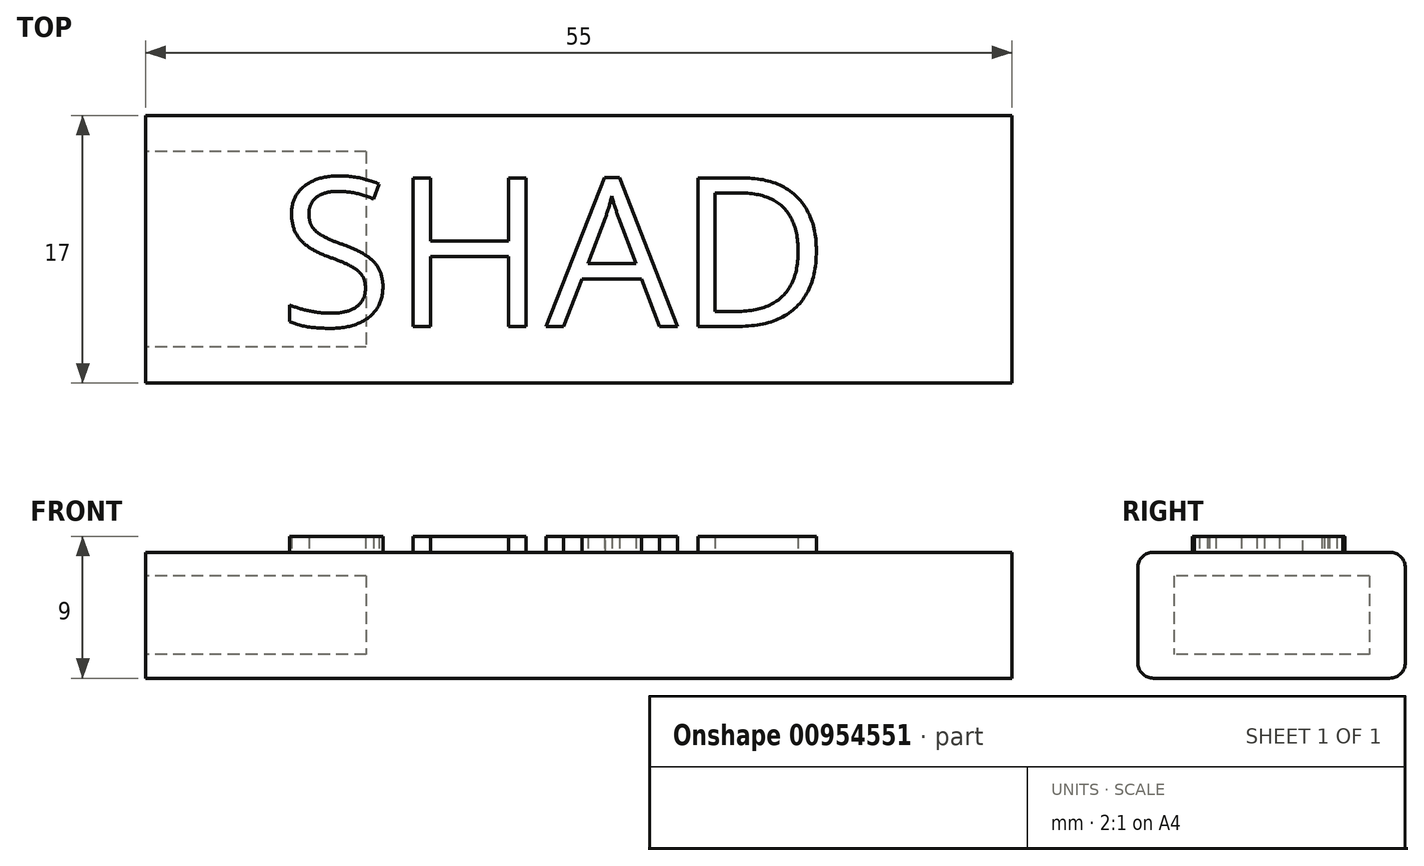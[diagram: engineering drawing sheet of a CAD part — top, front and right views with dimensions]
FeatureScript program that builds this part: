
annotation { "Feature Type Name" : "Feature", "Feature Type Description" : "" }
export const myFeature = defineFeature(function(context is Context, id is Id, definition is map)
    precondition{}
    {
        {
            var Q0;
            Q0=qCreatedBy(makeId("Front.planeOp"),FACE);
            var sketch = newSketch(context, id + "F0", { "sketchPlane" : qUnion([Q0])});
            skLineSegment(sketch, "E0.bottom", {"start": v(-7.5, 4) * mm, "end": v(7.5, 4) * mm});
            skLineSegment(sketch, "E0.top", {"start": v(-7.5, -4) * mm, "end": v(7.5, -4) * mm});
            skLineSegment(sketch, "E0.left", {"start": v(-8.5, 3) * mm, "end": v(-8.5, -3) * mm});
            skLineSegment(sketch, "E0.right", {"start": v(8.5, 3) * mm, "end": v(8.5, -3) * mm});
            skPoint(sketch, "E0.middle", {"position": v(0, 0) * mm});
            skPoint(sketch, "E1.visualSharp", {"position": v(-8.5, 4) * mm});
            skArc(sketch, "E1.filletArc", {"start": v(-7.5, 4) * mm, "mid": v(-8.2, 3.7) * mm, "end": v(-8.5, 3) * mm});
            skPoint(sketch, "E2.visualSharp", {"position": v(-8.5, -4) * mm});
            skArc(sketch, "E2.filletArc", {"start": v(-8.5, -3) * mm, "mid": v(-8.2, -3.7) * mm, "end": v(-7.5, -4) * mm});
            skPoint(sketch, "E3.visualSharp", {"position": v(8.5, 4) * mm});
            skArc(sketch, "E3.filletArc", {"start": v(8.5, 3) * mm, "mid": v(8.2, 3.7) * mm, "end": v(7.5, 4) * mm});
            skPoint(sketch, "E4.visualSharp", {"position": v(8.5, -4) * mm});
            skArc(sketch, "E4.filletArc", {"start": v(7.5, -4) * mm, "mid": v(8.2, -3.7) * mm, "end": v(8.5, -3) * mm});
            skSolve(sketch);
        }
        {
            var Q0;
            Q0=makeQuery(id+"F0.imprint","IMPRINT",FACE,{"disambiguationData":[TD([[makeQuery(id+"F0.imprint","IMPRINT",EDGE,{"derivedFrom":sQuery(id+"F0.wireOp",EDGE,"E0.bottom")}),-1.0]])]});
            extrude(context, id + "F1", {"entities" : qUnion([Q0]), "depth" : 55 * mm, "offsetDistance" : 25 * mm});
        }
        {
            var Q0;
            Q0=makeQuery(id+"F1.opExtrude","CAP_FACE",FACE,{"disambiguationData":[OSD([sQuery(id+"F0.wireOp",EDGE,"E0.bottom"),sQuery(id+"F0.wireOp",EDGE,"E0.top"),sQuery(id+"F0.wireOp",EDGE,"E0.left"),sQuery(id+"F0.wireOp",EDGE,"E0.right"),sQuery(id+"F0.wireOp",EDGE,"E1.filletArc"),sQuery(id+"F0.wireOp",EDGE,"E2.filletArc"),sQuery(id+"F0.wireOp",EDGE,"E3.filletArc"),sQuery(id+"F0.wireOp",EDGE,"E4.filletArc")])],"isStart":false});
            var sketch = newSketch(context, id + "F2", { "sketchPlane" : qUnion([Q0])});
            skLineSegment(sketch, "E5.bottom", {"start": v(-6.2, 2.5) * mm, "end": v(6.2, 2.5) * mm});
            skLineSegment(sketch, "E5.top", {"start": v(-6.2, -2.5) * mm, "end": v(6.2, -2.5) * mm});
            skLineSegment(sketch, "E5.left", {"start": v(-6.2, 2.5) * mm, "end": v(-6.2, -2.5) * mm});
            skLineSegment(sketch, "E5.right", {"start": v(6.2, 2.5) * mm, "end": v(6.2, -2.5) * mm});
            skPoint(sketch, "E5.middle", {"position": v(0, 0) * mm});
            skSolve(sketch);
        }
        {
            var Q0;
            Q0 = qSketchRegion(id + "F2", true);
            extrude(context, id + "F3", {"entities" : qUnion([Q0]), "operationType" : NewBodyOperationType.REMOVE, "oppositeDirection" : true, "depth" : 14 * mm, "offsetDistance" : 25 * mm});
        }
        {
            var Q0;
            Q0=makeQuery(id+"F1.opExtrude","SWEPT_BODY",BODY,{"disambiguationData":[OSD([sQuery(id+"F0.wireOp",EDGE,"E0.bottom"),sQuery(id+"F0.wireOp",EDGE,"E0.top"),sQuery(id+"F0.wireOp",EDGE,"E0.left"),sQuery(id+"F0.wireOp",EDGE,"E0.right"),sQuery(id+"F0.wireOp",EDGE,"E1.filletArc"),sQuery(id+"F0.wireOp",EDGE,"E2.filletArc"),sQuery(id+"F0.wireOp",EDGE,"E3.filletArc"),sQuery(id+"F0.wireOp",EDGE,"E4.filletArc")])]});
            var Q1;
            Q1=makeQuery(id+"F1.opExtrude","CAP_EDGE",EDGE,{"disambiguationData":[OSD([sQuery(id+"F0.wireOp",EDGE,"E0.right")])],"isStart":false});
            transform(context, id + "F4", {"entities" : qUnion([Q0]), "transformType" : TransformType.ROTATION, "transformAxis" : qUnion([Q1]), "angle" : 90 * degree, "makeCopy" : false});
        }
        {
            var Q0;
            Q0=makeQuery(id+"F1.opExtrude","SWEPT_FACE",FACE,{"disambiguationData":[OSD([sQuery(id+"F0.wireOp",EDGE,"E0.bottom")])]});
            var sketch = newSketch(context, id + "F5", { "sketchPlane" : qUnion([Q0])});
            skText(sketch, "E6", { "text": "SHAD", "fontName": "OpenSans-Regular.ttf"});
            const initialGuessF5  = {"E6": [0.01695, -0.0514, 1, 0, 0.0095]};
            skSetInitialGuess(sketch, initialGuessF5);
            skSolve(sketch);
        }
        {
            var Q0;
            Q0 = qSketchRegion(id + "F5", true);
            extrude(context, id + "F6", {"entities" : qUnion([Q0]), "operationType" : NewBodyOperationType.ADD, "depth" : 1 * mm, "offsetDistance" : 25 * mm});
        }
    });
